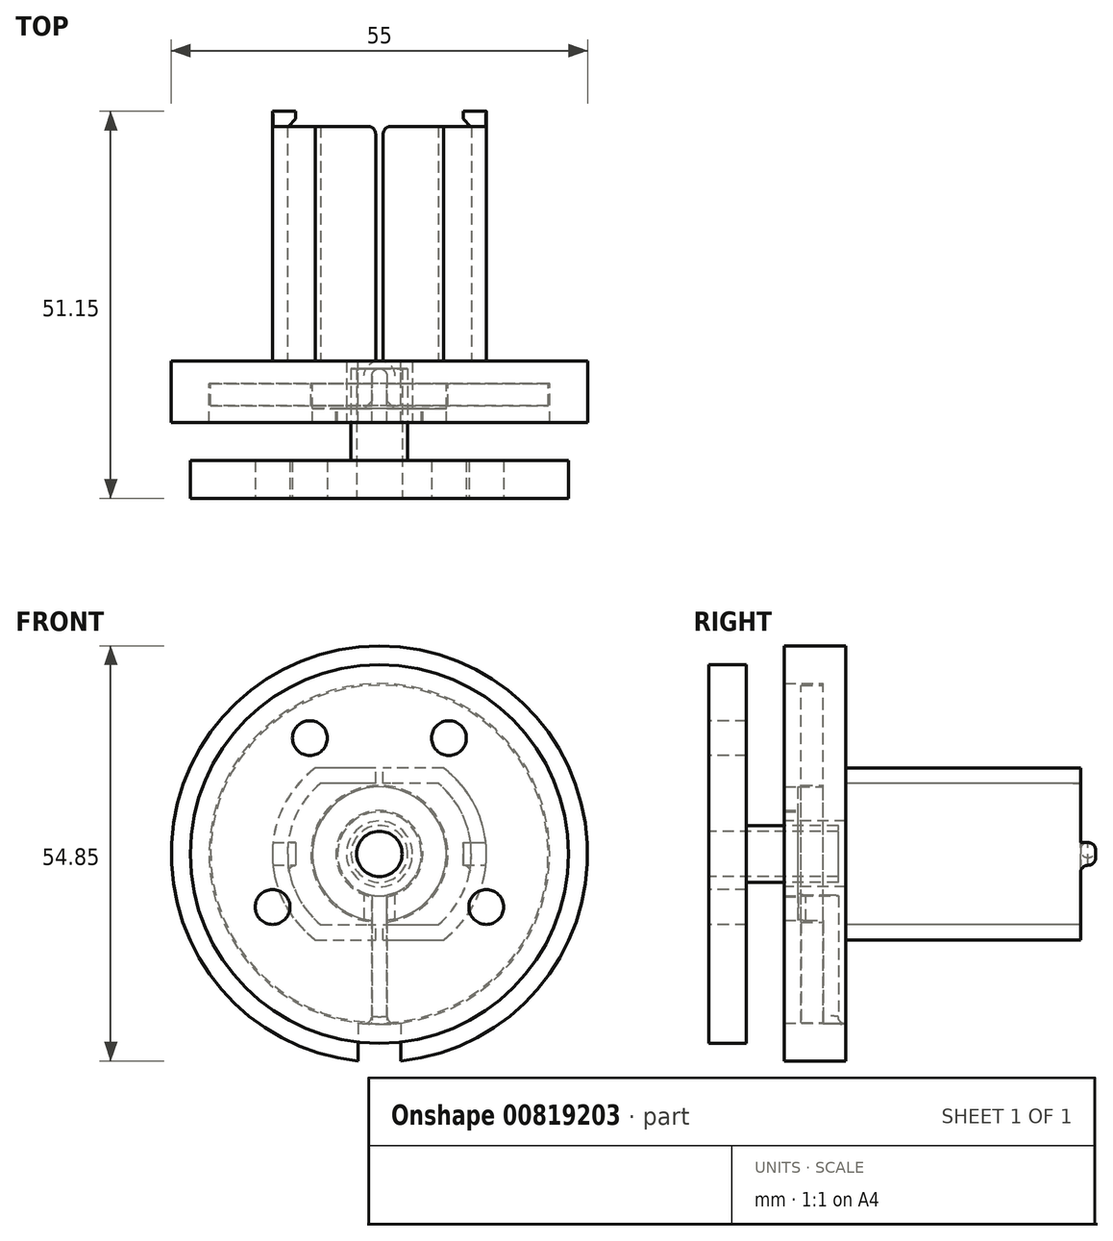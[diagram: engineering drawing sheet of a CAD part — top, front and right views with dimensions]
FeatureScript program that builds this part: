
annotation { "Feature Type Name" : "Feature", "Feature Type Description" : "" }
export const myFeature = defineFeature(function(context is Context, id is Id, definition is map)
    precondition{}
    {
        {
            var Q0;
            Q0=qCreatedBy(makeId("Front.planeOp"),FACE);
            var sketch = newSketch(context, id + "F0", { "sketchPlane" : qUnion([Q0])});
            skCircle(sketch, "E0", {"center": v(-32.51, 36.23) * mm, "radius": 22.3 * mm});
            skCircle(sketch, "E1", {"center": v(-32.51, 36.23) * mm, "radius": 9.05 * mm});
            skCircle(sketch, "E2", {"center": v(-32.51, 36.23) * mm, "radius": 27.5 * mm});
            skSolve(sketch);
        }
        {
            var Q0;
            Q0=makeQuery(id+"F0.imprint","IMPRINT",FACE,{"disambiguationData":[TD([[makeQuery(id+"F0.imprint","IMPRINT",EDGE,{"derivedFrom":sQuery(id+"F0.wireOp",EDGE,"E0")}),1.0]])]});
            extrude(context, id + "F1", {"entities" : qUnion([Q0]), "depth" : 2.9 * mm, "offsetDistance" : 25 * mm});
        }
        {
            var Q0;
            Q0=makeQuery(id+"F1.opExtrude","CAP_FACE",FACE,{"disambiguationData":[OSD([sQuery(id+"F0.wireOp",EDGE,"E0"),sQuery(id+"F0.wireOp",EDGE,"E1")])],"isStart":false});
            cPlane(context, id + "F2", {"entities" : qUnion([Q0]), "cplaneType" : CPlaneType.OFFSET, "offset" : .4 * mm, "width" : 150 * mm, "height" : 150 * mm});
        }
        {
            var Q0;
            Q0=qCreatedBy(id+"F2.planeOp",FACE);
            var sketch = newSketch(context, id + "F3", { "sketchPlane" : qUnion([Q0])});
            skCircle(sketch, "E3.0", {"center": v(-32.51, 36.23) * mm, "radius": 9.05 * mm});
            skCircle(sketch, "E4", {"center": v(-32.51, 36.23) * mm, "radius": 12.7 * mm});
            skCircle(sketch, "E5", {"center": v(-32.51, 36.23) * mm, "radius": 5.75 * mm});
            skSolve(sketch);
        }
        {
            var Q0;
            Q0=makeQuery(id+"F3.imprint","IMPRINT",FACE,{"disambiguationData":[TD([[makeQuery(id+"F3.imprint","IMPRINT",EDGE,{"derivedFrom":sQuery(id+"F3.wireOp",EDGE,"E3.0")}),1.0]])]});
            var Q1;
            Q1=makeQuery(id+"F3.imprint","IMPRINT",FACE,{"disambiguationData":[TD([[makeQuery(id+"F3.imprint","IMPRINT",EDGE,{"derivedFrom":sQuery(id+"F3.wireOp",EDGE,"E3.0")}),-1.0]])]});
            extrude(context, id + "F4", {"entities" : qUnion([Q0, Q1]), "depth" : 1.85 * mm, "offsetDistance" : 25 * mm});
        }
        {
            var Q0;
            Q0=makeQuery(id+"F0.imprint","IMPRINT",FACE,{"disambiguationData":[TD([[makeQuery(id+"F0.imprint","IMPRINT",EDGE,{"derivedFrom":sQuery(id+"F0.wireOp",EDGE,"E0")}),-1.0]])]});
            var Q1;
            Q1=makeQuery(id+"F0.imprint","IMPRINT",FACE,{"disambiguationData":[TD([[makeQuery(id+"F0.imprint","IMPRINT",EDGE,{"derivedFrom":sQuery(id+"F0.wireOp",EDGE,"E0")}),1.0]])]});
            var Q2;
            Q2=makeQuery(id+"F0.imprint","IMPRINT",FACE,{"disambiguationData":[TD([[makeQuery(id+"F0.imprint","IMPRINT",EDGE,{"derivedFrom":sQuery(id+"F0.wireOp",EDGE,"E1")}),1.0]])]});
            var Q3;
            Q3=makeQuery(id+"F4.opExtrude","CAP_FACE",FACE,{"disambiguationData":[OSD([sQuery(id+"F3.wireOp",EDGE,"E4"),sQuery(id+"F3.wireOp",EDGE,"E5")])],"isStart":false});
            extrude(context, id + "F5", {"entities" : qUnion([Q0, Q1, Q2]), "endBound" : BoundingType.UP_TO_SURFACE, "depth" : 25 * mm, "endBoundEntityFace" : qUnion([Q3]), "offsetDistance" : 25 * mm, "hasSecondDirection" : true, "secondDirectionOppositeDirection" : true, "secondDirectionDepth" : 3 * mm});
        }
        {
            var Q0;
            Q0=makeQuery(id+"F1.opExtrude","SWEPT_BODY",BODY,{"disambiguationData":[OSD([sQuery(id+"F0.wireOp",EDGE,"E0"),sQuery(id+"F0.wireOp",EDGE,"E1")])]});
            var Q1;
            Q1=makeQuery(id+"F4.opExtrude","SWEPT_BODY",BODY,{"disambiguationData":[OSD([sQuery(id+"F3.wireOp",EDGE,"E4"),sQuery(id+"F3.wireOp",EDGE,"E5")])]});
            var Q2;
            Q2=makeQuery(id+"F5.opExtrude","SWEPT_BODY",BODY,{"disambiguationData":[OSD([sQuery(id+"F0.wireOp",EDGE,"E2")])]});
            var Q3;
            Q3=makeQuery(id+"F4.opExtrude","SWEPT_FACE",FACE,{"disambiguationData":[OSD([sQuery(id+"F3.wireOp",EDGE,"E5")])]});
            var Q4;
            Q4=makeQuery(id+"F4.opExtrude","SWEPT_FACE",FACE,{"disambiguationData":[OSD([sQuery(id+"F3.wireOp",EDGE,"E4")])]});
            var Q5;
            Q5=makeQuery(id+"F1.opExtrude","SWEPT_FACE",FACE,{"disambiguationData":[OSD([sQuery(id+"F0.wireOp",EDGE,"E0")])]});
            var Q6;
            Q6=makeQuery(id+"F1.opExtrude","SWEPT_FACE",FACE,{"disambiguationData":[OSD([sQuery(id+"F0.wireOp",EDGE,"E1")])]});
            booleanBodies(context, id + "F6", {"operationType" : BooleanOperationType.SUBTRACTION, "tools" : qUnion([Q0, Q1]), "targets" : qUnion([Q2]), "offset" : true, "entitiesToOffset" : qUnion([Q3, Q4, Q5, Q6]), "offsetDistance" : .2 * mm, "keepTools" : true});
        }
        {
            var Q0;
            Q0=makeQuery(id+"F6.opBoolean","COPY",FACE,{"derivedFrom":makeQuery(id+"F1.opExtrude","CAP_FACE",FACE,{"disambiguationData":[OSD([sQuery(id+"F0.wireOp",EDGE,"E0"),sQuery(id+"F0.wireOp",EDGE,"E1")])],"isStart":false})});
            var Q1;
            Q1=makeQuery(id+"F6.tempBoolean.opBoolean","COPY",FACE,{"derivedFrom":makeQuery(id+"F6.offsetTempBody.opPattern","COPY",FACE,{"derivedFrom":makeQuery(id+"F1.opExtrude","CAP_FACE",FACE,{"disambiguationData":[OSD([sQuery(id+"F0.wireOp",EDGE,"E0"),sQuery(id+"F0.wireOp",EDGE,"E1")])],"isStart":false}),"instanceName":"1"})});
            extrude(context, id + "F7", {"entities" : qUnion([Q0, Q1]), "operationType" : NewBodyOperationType.REMOVE, "endBound" : BoundingType.THROUGH_ALL, "oppositeDirection" : true, "depth" : 25 * mm, "offsetDistance" : 25 * mm});
        }
        {
            var Q0;
            Q0=makeQuery(id+"F6.tempBoolean.opBoolean","SPLIT",FACE,{"disambiguationData":[TD([makeQuery(id+"F6.offsetTempBody.opPattern","COPY",FACE,{"derivedFrom":makeQuery(id+"F4.opExtrude","SWEPT_FACE",FACE,{"disambiguationData":[OSD([sQuery(id+"F3.wireOp",EDGE,"E5")])]}),"instanceName":"1"})])],"derivedFrom":makeQuery(id+"F5.opExtrude","CAP_FACE",FACE,{"disambiguationData":[OSD([sQuery(id+"F0.wireOp",EDGE,"E2")])],"isStart":false})});
            var sketch = newSketch(context, id + "F8", { "sketchPlane" : qUnion([Q0])});
            skCircle(sketch, "E6.0", {"center": v(-32.51, 36.23) * mm, "radius": 5.55 * mm});
            skCircle(sketch, "E7", {"center": v(-32.51, 36.23) * mm, "radius": 4.35 * mm});
            skPoint(sketch, "E8", {"position": v(-36.86, 36.23) * mm});
            skPoint(sketch, "E9", {"position": v(-38.06, 36.23) * mm});
            skSolve(sketch);
        }
        {
            var Q0;
            Q0=makeQuery(id+"F8.imprint","IMPRINT",FACE,{"disambiguationData":[TD([[makeQuery(id+"F8.imprint","IMPRINT",EDGE,{"derivedFrom":sQuery(id+"F8.wireOp",EDGE,"E7")}),1.0]])]});
            extrude(context, id + "F9", {"entities" : qUnion([Q0]), "operationType" : NewBodyOperationType.REMOVE, "endBound" : BoundingType.THROUGH_ALL, "oppositeDirection" : true, "depth" : 25 * mm, "offsetDistance" : 25 * mm});
        }
        {
            var Q0;
            Q0=makeQuery(id+"F6.tempBoolean.opBoolean","SPLIT",FACE,{"disambiguationData":[TD([makeQuery(id+"F6.offsetTempBody.opPattern","COPY",FACE,{"derivedFrom":makeQuery(id+"F4.opExtrude","SWEPT_FACE",FACE,{"disambiguationData":[OSD([sQuery(id+"F3.wireOp",EDGE,"E5")])]}),"instanceName":"1"})])],"derivedFrom":makeQuery(id+"F5.opExtrude","CAP_FACE",FACE,{"disambiguationData":[OSD([sQuery(id+"F0.wireOp",EDGE,"E2")])],"isStart":false})});
            var sketch = newSketch(context, id + "F10", { "sketchPlane" : qUnion([Q0])});
            skCircle(sketch, "E10.0", {"center": v(-32.51, 36.23) * mm, "radius": 4.35 * mm});
            skCircle(sketch, "E11", {"center": v(-32.51, 36.23) * mm, "radius": 3 * mm});
            skCircle(sketch, "E12", {"center": v(-32.51, 36.23) * mm, "radius": 3.75 * mm});
            skPoint(sketch, "E13", {"position": v(-35.51, 36.23) * mm});
            skPoint(sketch, "E14", {"position": v(-36.26, 36.23) * mm});
            skPoint(sketch, "E15", {"position": v(-36.86, 36.23) * mm});
            skSolve(sketch);
        }
        {
            var Q0;
            Q0=makeQuery(id+"F10.imprint","IMPRINT",FACE,{"disambiguationData":[TD([[makeQuery(id+"F10.imprint","IMPRINT",EDGE,{"derivedFrom":sQuery(id+"F10.wireOp",EDGE,"E11")}),-1.0]])]});
            var Q1;
            Q1=makeQuery(id+"F5.opExtrude","CAP_FACE",FACE,{"disambiguationData":[OSD([sQuery(id+"F0.wireOp",EDGE,"E2")])],"isStart":true});
            extrude(context, id + "F11", {"entities" : qUnion([Q0]), "endBound" : BoundingType.UP_TO_SURFACE, "oppositeDirection" : true, "depth" : 25 * mm, "endBoundEntityFace" : qUnion([Q1]), "hasOffset" : true, "offsetDistance" : 1 * mm, "hasSecondDirection" : true, "secondDirectionOppositeDirection" : false, "secondDirectionDepth" : 5 * mm});
        }
        {
            var Q0;
            Q0=makeQuery(id+"F11.opExtrude","CAP_FACE",FACE,{"disambiguationData":[OSD([sQuery(id+"F10.wireOp",EDGE,"E11"),sQuery(id+"F10.wireOp",EDGE,"E12")])],"isStart":true});
            var sketch = newSketch(context, id + "F12", { "sketchPlane" : qUnion([Q0])});
            skCircle(sketch, "E16.0", {"center": v(-32.51, 36.23) * mm, "radius": 3 * mm});
            skCircle(sketch, "E17", {"center": v(-32.51, 36.23) * mm, "radius": 25 * mm});
            skSolve(sketch);
        }
        {
            var Q0;
            Q0=makeQuery(id+"F12.imprint","IMPRINT",FACE,{"disambiguationData":[TD([[makeQuery(id+"F12.imprint","IMPRINT",EDGE,{"derivedFrom":sQuery(id+"F12.wireOp",EDGE,"E17")}),1.0]])]});
            var Q1;
            Q1=makeQuery(id+"F12.imprint","IMPRINT",FACE,{"disambiguationData":[TD([[makeQuery(id+"F12.imprint","IMPRINT",EDGE,{"derivedFrom":sQuery(id+"F12.wireOp",EDGE,"E16.0")}),-1.0]])]});
            extrude(context, id + "F13", {"entities" : qUnion([Q0, Q1]), "operationType" : NewBodyOperationType.ADD, "depth" : 5 * mm, "offsetDistance" : 25 * mm});
        }
        {
            var Q0;
            Q0=makeQuery(id+"F13.opExtrude","CAP_FACE",FACE,{"disambiguationData":[OSD([sQuery(id+"F12.wireOp",EDGE,"E16.0"),sQuery(id+"F12.wireOp",EDGE,"E17")])],"isStart":false});
            var sketch = newSketch(context, id + "F14", { "sketchPlane" : qUnion([Q0])});
            skCircle(sketch, "E18", {"center": v(-41.7, 51.54) * mm, "radius": 2.3 * mm});
            skCircle(sketch, "E19", {"center": v(-23.32, 51.54) * mm, "radius": 2.3 * mm});
            skCircle(sketch, "E20", {"center": v(-46.63, 29.22) * mm, "radius": 2.3 * mm});
            skCircle(sketch, "E21", {"center": v(-18.4, 29.22) * mm, "radius": 2.3 * mm});
            skLineSegment(sketch, "E22", {"start": v(-46.63, 29.22) * mm, "end": v(-18.4, 29.22) * mm, "construction": true});
            skLineSegment(sketch, "E23", {"start": v(-41.7, 51.54) * mm, "end": v(-23.32, 51.54) * mm, "construction": true});
            skPoint(sketch, "E24", {"position": v(-32.51, 51.54) * mm});
            skPoint(sketch, "E25", {"position": v(-32.51, 29.22) * mm});
            skCircle(sketch, "E26.0", {"center": v(-32.51, 36.23) * mm, "radius": 3 * mm});
            skSolve(sketch);
        }
        {
            var Q0;
            Q0=makeQuery(id+"F14.imprint","IMPRINT",FACE,{"disambiguationData":[TD([[makeQuery(id+"F14.imprint","IMPRINT",EDGE,{"derivedFrom":sQuery(id+"F14.wireOp",EDGE,"E20")}),1.0]])]});
            var Q1;
            Q1=makeQuery(id+"F14.imprint","IMPRINT",FACE,{"disambiguationData":[TD([[makeQuery(id+"F14.imprint","IMPRINT",EDGE,{"derivedFrom":sQuery(id+"F14.wireOp",EDGE,"E18")}),1.0]])]});
            var Q2;
            Q2=makeQuery(id+"F14.imprint","IMPRINT",FACE,{"disambiguationData":[TD([[makeQuery(id+"F14.imprint","IMPRINT",EDGE,{"derivedFrom":sQuery(id+"F14.wireOp",EDGE,"E19")}),1.0]])]});
            var Q3;
            Q3=makeQuery(id+"F14.imprint","IMPRINT",FACE,{"disambiguationData":[TD([[makeQuery(id+"F14.imprint","IMPRINT",EDGE,{"derivedFrom":sQuery(id+"F14.wireOp",EDGE,"E21")}),1.0]])]});
            extrude(context, id + "F15", {"entities" : qUnion([Q0, Q1, Q2, Q3]), "operationType" : NewBodyOperationType.REMOVE, "endBound" : BoundingType.UP_TO_NEXT, "oppositeDirection" : true, "depth" : 25 * mm, "offsetDistance" : 25 * mm});
        }
        {
            var Q0;
            Q0=qCreatedBy(makeId("Top.planeOp"),FACE);
            var sketch = newSketch(context, id + "F16", { "sketchPlane" : qUnion([Q0])});
            skLineSegment(sketch, "E27.bottom", {"start": v(-35.34, -7.22) * mm, "end": v(-29.7, -7.22) * mm});
            skLineSegment(sketch, "E27.top", {"start": v(-35.34, 5.14) * mm, "end": v(-29.7, 5.14) * mm});
            skLineSegment(sketch, "E27.left", {"start": v(-35.34, -7.22) * mm, "end": v(-35.34, 5.14) * mm});
            skLineSegment(sketch, "E27.right", {"start": v(-29.7, -7.22) * mm, "end": v(-29.7, 5.14) * mm});
            skLineSegment(sketch, "E28.0", {"start": v(-5.01, -5.15) * mm, "end": v(-60.01, -5.15) * mm});
            skPoint(sketch, "E29", {"position": v(-32.51, -5.15) * mm});
            skPoint(sketch, "E30", {"position": v(-32.51, -7.22) * mm});
            skSolve(sketch);
        }
        {
            var Q0;
            {var subQ0=sQuery(id+"F16.wireOp",EDGE,"E27.top");Q0=makeQuery(id+"F16.imprint","IMPRINT",FACE,{"disambiguationData":[TD([[makeQuery(id+"F16.imprint","IMPRINT",EDGE,{"derivedFrom":subQ0}),-1.0]])]});}
            var Q1;
            {var subQ0=sQuery(id+"F0.wireOp",EDGE,"E0");Q1=makeQuery(id+"F7.boolean.opBoolean","MERGE",FACE,{"derivedFrom":[makeQuery(id+"F6.tempBoolean.opBoolean","COPY",FACE,{"derivedFrom":makeQuery(id+"F6.offsetTempBody.opPattern","COPY",FACE,{"derivedFrom":makeQuery(id+"F1.opExtrude","SWEPT_FACE",FACE,{"disambiguationData":[OSD([subQ0])]}),"instanceName":"1"})}),makeQuery(id+"F7.opExtrude","SWEPT_FACE",FACE,{"disambiguationData":[OSD([subQ0])]})]});}
            extrude(context, id + "F17", {"entities" : qUnion([Q0]), "operationType" : NewBodyOperationType.REMOVE, "endBound" : BoundingType.UP_TO_SURFACE, "depth" : 20 * mm, "endBoundEntityFace" : qUnion([Q1]), "offsetDistance" : 25 * mm});
        }
        {
            var Q0;
            Q0=makeQuery(id+"F5.opExtrude","CAP_FACE",FACE,{"disambiguationData":[OSD([sQuery(id+"F0.wireOp",EDGE,"E2")])],"isStart":true});
            var sketch = newSketch(context, id + "F18", { "sketchPlane" : qUnion([Q0])});
            skArc(sketch, "E31", {"start": v(40.27, 26.88) * mm, "mid": v(44.66, 36.23) * mm, "end": v(40.27, 45.58) * mm});
            skLineSegment(sketch, "E32", {"start": v(40.27, 26.88) * mm, "end": v(24.75, 26.88) * mm});
            skLineSegment(sketch, "E33", {"start": v(24.75, 45.58) * mm, "end": v(40.27, 45.58) * mm});
            skArc(sketch, "E34.trimOffspring", {"start": v(24.75, 45.58) * mm, "mid": v(20.36, 36.23) * mm, "end": v(24.75, 26.88) * mm});
            skLineSegment(sketch, "E35.0", {"start": v(40.96, 24.88) * mm, "end": v(24.06, 24.88) * mm});
            skArc(sketch, "E35.1", {"start": v(40.96, 24.88) * mm, "mid": v(46.66, 36.23) * mm, "end": v(40.96, 47.58) * mm});
            skLineSegment(sketch, "E35.2", {"start": v(24.06, 47.58) * mm, "end": v(40.96, 47.58) * mm});
            skArc(sketch, "E35.3", {"start": v(24.06, 47.58) * mm, "mid": v(18.36, 36.23) * mm, "end": v(24.06, 24.88) * mm});
            skLineSegment(sketch, "E36", {"start": v(32.51, 24.88) * mm, "end": v(32.51, 47.58) * mm, "construction": true});
            skArc(sketch, "E37.0.startCap", {"start": v(33.01, 24.88) * mm, "mid": v(32.51, 24.38) * mm, "end": v(32.01, 24.88) * mm, "construction": true});
            skArc(sketch, "E37.0.endCap", {"start": v(32.01, 47.58) * mm, "mid": v(32.51, 48.08) * mm, "end": v(33.01, 47.58) * mm, "construction": true});
            skLineSegment(sketch, "E37.0.left", {"start": v(32.01, 24.88) * mm, "end": v(32.01, 47.58) * mm});
            skLineSegment(sketch, "E37.0.right", {"start": v(33.01, 24.88) * mm, "end": v(33.01, 47.58) * mm});
            skSolve(sketch);
        }
        {
            var Q0;
            Q0=makeQuery(id+"F18.imprint","IMPRINT",FACE,{"disambiguationData":[TD([[makeQuery(id+"F18.imprint","IMPRINT",EDGE,{"derivedFrom":sQuery(id+"F18.wireOp",EDGE,"E31")}),-1.0]])]});
            var Q1;
            {var subQ4=sQuery(id+"F18.wireOp",EDGE,"E34.trimOffspring");Q1=makeQuery(id+"F18.imprint","IMPRINT",FACE,{"disambiguationData":[TD([[makeQuery(id+"F18.imprint","IMPRINT",EDGE,{"derivedFrom":subQ4}),-1.0]])]});}
            extrude(context, id + "F19", {"entities" : qUnion([Q0, Q1]), "operationType" : NewBodyOperationType.ADD, "depth" : 31 * mm, "offsetDistance" : 25 * mm});
        }
        {
            var Q0;
            Q0=makeQuery(id+"F19.opExtrude","CAP_FACE",FACE,{"disambiguationData":[OSD([sQuery(id+"F18.wireOp",EDGE,"E31"),sQuery(id+"F18.wireOp",EDGE,"E32"),sQuery(id+"F18.wireOp",EDGE,"E33"),sQuery(id+"F18.wireOp",EDGE,"E35.0"),sQuery(id+"F18.wireOp",EDGE,"E35.1"),sQuery(id+"F18.wireOp",EDGE,"E35.2"),sQuery(id+"F18.wireOp",EDGE,"E37.0.right")])],"isStart":false});
            var sketch = newSketch(context, id + "F20", { "sketchPlane" : qUnion([Q0])});
            skArc(sketch, "E38.0", {"start": v(24.06, 47.58) * mm, "mid": v(18.36, 36.23) * mm, "end": v(24.06, 24.88) * mm});
            skArc(sketch, "E38.1", {"start": v(40.96, 24.88) * mm, "mid": v(46.66, 36.23) * mm, "end": v(40.96, 47.58) * mm});
            skLineSegment(sketch, "E39", {"start": v(46.66, 36.23) * mm, "end": v(43.57, 36.23) * mm, "construction": true});
            skArc(sketch, "E40.0.startCap", {"start": v(46.66, 37.73) * mm, "mid": v(48.16, 36.23) * mm, "end": v(46.66, 34.73) * mm, "construction": true});
            skArc(sketch, "E40.0.endCap", {"start": v(18.36, 34.73) * mm, "mid": v(16.86, 36.23) * mm, "end": v(18.36, 37.73) * mm, "construction": true});
            skLineSegment(sketch, "E40.0.left", {"start": v(46.66, 34.73) * mm, "end": v(43.57, 34.73) * mm});
            skLineSegment(sketch, "E40.0.right", {"start": v(46.66, 37.73) * mm, "end": v(43.57, 37.73) * mm});
            skLineSegment(sketch, "E41.left", {"start": v(43.57, 37.73) * mm, "end": v(43.57, 34.73) * mm});
            skLineSegment(sketch, "E41.right", {"start": v(21.46, 37.73) * mm, "end": v(21.46, 34.73) * mm});
            skLineSegment(sketch, "E42.trimOffspring", {"start": v(21.46, 34.73) * mm, "end": v(18.36, 34.73) * mm});
            skLineSegment(sketch, "E43.trimOffspring", {"start": v(21.46, 37.73) * mm, "end": v(18.36, 37.73) * mm});
            skLineSegment(sketch, "E44.trimOffspring", {"start": v(21.46, 36.23) * mm, "end": v(18.36, 36.23) * mm, "construction": true});
            skPoint(sketch, "E45", {"position": v(44.57, 34.73) * mm});
            skSolve(sketch);
        }
        {
            var Q0;
            {var subQ0=sQuery(id+"F20.wireOp",EDGE,"E41.left");Q0=makeQuery(id+"F20.imprint","IMPRINT",FACE,{"disambiguationData":[TD([[makeQuery(id+"F20.imprint","IMPRINT",EDGE,{"derivedFrom":subQ0}),1.0]])]});}
            var Q1;
            {var subQ0=sQuery(id+"F20.wireOp",EDGE,"E40.0.left");var subQ1=sQuery(id+"F20.wireOp",EDGE,"E38.1");var subQ2=makeQuery(id+"F20.imprint","INTERSECT",VERTEX,{"derivedFrom":[subQ1,subQ0]});Q1=makeQuery(id+"F20.imprint","IMPRINT",FACE,{"disambiguationData":[TD([[makeQuery(id+"F20.imprint","IMPRINT",EDGE,{"disambiguationData":[TD([[subQ2,-1.0]])],"derivedFrom":subQ1}),1.0]])]});}
            var Q2;
            {var subQ5=sQuery(id+"F20.wireOp",EDGE,"E41.right");Q2=makeQuery(id+"F20.imprint","IMPRINT",FACE,{"disambiguationData":[TD([[makeQuery(id+"F20.imprint","IMPRINT",EDGE,{"derivedFrom":subQ5}),-1.0]])]});}
            extrude(context, id + "F21", {"entities" : qUnion([Q0, Q1, Q2]), "operationType" : NewBodyOperationType.ADD, "depth" : 2 * mm, "offsetDistance" : 25 * mm});
        }
        {
            var Q0;
            Q0=makeQuery(id+"F21.opExtrude","CAP_EDGE",EDGE,{"disambiguationData":[OSD([sQuery(id+"F20.wireOp",EDGE,"E41.left")])],"isStart":true});
            var Q1;
            Q1=makeQuery(id+"F21.opExtrude","CAP_EDGE",EDGE,{"disambiguationData":[OSD([sQuery(id+"F20.wireOp",EDGE,"E41.right")])],"isStart":true});
            chamfer(context, id + "F22", {"entities" : qUnion([Q0, Q1]), "width" : 1 * mm, "tangentPropagation" : true});
        }
        {
            var Q0;
            {var subQ0=sQuery(id+"F20.wireOp",EDGE,"E40.0.right");Q0=makeQuery(id+"F21.boolean.opBoolean","SPLIT",EDGE,{"disambiguationData":[topologyDisambiguationEdgeConnected([makeQuery(id+"F19.opExtrude","CAP_FACE",FACE,{"disambiguationData":[OSD([sQuery(id+"F18.wireOp",EDGE,"E31"),sQuery(id+"F18.wireOp",EDGE,"E32"),sQuery(id+"F18.wireOp",EDGE,"E33"),sQuery(id+"F18.wireOp",EDGE,"E35.0"),sQuery(id+"F18.wireOp",EDGE,"E35.1"),sQuery(id+"F18.wireOp",EDGE,"E35.2"),sQuery(id+"F18.wireOp",EDGE,"E37.0.right")])],"isStart":false})])],"derivedFrom":makeQuery(id+"F21.opExtrude","CAP_EDGE",EDGE,{"disambiguationData":[OSD([subQ0])],"isStart":true})});}
            var Q1;
            {var subQ0=sQuery(id+"F20.wireOp",EDGE,"E43.trimOffspring");Q1=makeQuery(id+"F21.boolean.opBoolean","SPLIT",EDGE,{"disambiguationData":[topologyDisambiguationEdgeConnected([makeQuery(id+"F19.opExtrude","CAP_FACE",FACE,{"disambiguationData":[OSD([sQuery(id+"F18.wireOp",EDGE,"E32"),sQuery(id+"F18.wireOp",EDGE,"E33"),sQuery(id+"F18.wireOp",EDGE,"E34.trimOffspring"),sQuery(id+"F18.wireOp",EDGE,"E35.0"),sQuery(id+"F18.wireOp",EDGE,"E35.2"),sQuery(id+"F18.wireOp",EDGE,"E35.3"),sQuery(id+"F18.wireOp",EDGE,"E37.0.left")])],"isStart":false})])],"derivedFrom":makeQuery(id+"F21.opExtrude","CAP_EDGE",EDGE,{"disambiguationData":[OSD([subQ0])],"isStart":true})});}
            var Q2;
            {var subQ0=sQuery(id+"F20.wireOp",EDGE,"E42.trimOffspring");Q2=makeQuery(id+"F21.boolean.opBoolean","SPLIT",EDGE,{"disambiguationData":[topologyDisambiguationEdgeConnected([makeQuery(id+"F19.opExtrude","CAP_FACE",FACE,{"disambiguationData":[OSD([sQuery(id+"F18.wireOp",EDGE,"E32"),sQuery(id+"F18.wireOp",EDGE,"E33"),sQuery(id+"F18.wireOp",EDGE,"E34.trimOffspring"),sQuery(id+"F18.wireOp",EDGE,"E35.0"),sQuery(id+"F18.wireOp",EDGE,"E35.2"),sQuery(id+"F18.wireOp",EDGE,"E35.3"),sQuery(id+"F18.wireOp",EDGE,"E37.0.left")])],"isStart":false})])],"derivedFrom":makeQuery(id+"F21.opExtrude","CAP_EDGE",EDGE,{"disambiguationData":[OSD([subQ0])],"isStart":true})});}
            var Q3;
            {var subQ0=sQuery(id+"F20.wireOp",EDGE,"E40.0.left");Q3=makeQuery(id+"F21.boolean.opBoolean","SPLIT",EDGE,{"disambiguationData":[topologyDisambiguationEdgeConnected([makeQuery(id+"F19.opExtrude","CAP_FACE",FACE,{"disambiguationData":[OSD([sQuery(id+"F18.wireOp",EDGE,"E31"),sQuery(id+"F18.wireOp",EDGE,"E32"),sQuery(id+"F18.wireOp",EDGE,"E33"),sQuery(id+"F18.wireOp",EDGE,"E35.0"),sQuery(id+"F18.wireOp",EDGE,"E35.1"),sQuery(id+"F18.wireOp",EDGE,"E35.2"),sQuery(id+"F18.wireOp",EDGE,"E37.0.right")])],"isStart":false})])],"derivedFrom":makeQuery(id+"F21.opExtrude","CAP_EDGE",EDGE,{"disambiguationData":[OSD([subQ0])],"isStart":true})});}
            var Q4;
            Q4=makeQuery(id+"F21.opExtrude","CAP_EDGE",EDGE,{"disambiguationData":[OSD([sQuery(id+"F20.wireOp",EDGE,"E40.0.left")])],"isStart":false});
            var Q5;
            Q5=makeQuery(id+"F21.opExtrude","CAP_EDGE",EDGE,{"disambiguationData":[OSD([sQuery(id+"F20.wireOp",EDGE,"E40.0.right")])],"isStart":false});
            var Q6;
            Q6=makeQuery(id+"F21.opExtrude","CAP_EDGE",EDGE,{"disambiguationData":[OSD([sQuery(id+"F20.wireOp",EDGE,"E42.trimOffspring")])],"isStart":false});
            var Q7;
            Q7=makeQuery(id+"F21.opExtrude","CAP_EDGE",EDGE,{"disambiguationData":[OSD([sQuery(id+"F20.wireOp",EDGE,"E43.trimOffspring")])],"isStart":false});
            var Q8;
            {var subQ0=sQuery(id+"F18.wireOp",EDGE,"E37.0.right");Q8=makeQuery(id+"F19.opExtrude","CAP_EDGE",EDGE,{"disambiguationData":[OSD([subQ0]),TDD([makeQuery(id+"F18.imprint","IMPRINT",EDGE,{"disambiguationData":[TD([[makeQuery(id+"F18.imprint","INTERSECT",VERTEX,{"derivedFrom":[sQuery(id+"F18.wireOp",EDGE,"E35.0"),subQ0]}),-1.0]])],"derivedFrom":subQ0})])],"isStart":false});}
            var Q9;
            {var subQ0=sQuery(id+"F18.wireOp",EDGE,"E37.0.left");Q9=makeQuery(id+"F19.opExtrude","CAP_EDGE",EDGE,{"disambiguationData":[OSD([subQ0]),TDD([makeQuery(id+"F18.imprint","IMPRINT",EDGE,{"disambiguationData":[TD([[makeQuery(id+"F18.imprint","INTERSECT",VERTEX,{"derivedFrom":[sQuery(id+"F18.wireOp",EDGE,"E35.0"),subQ0]}),-1.0]])],"derivedFrom":subQ0})])],"isStart":false});}
            var Q10;
            {var subQ0=sQuery(id+"F18.wireOp",EDGE,"E37.0.left");Q10=makeQuery(id+"F19.opExtrude","CAP_EDGE",EDGE,{"disambiguationData":[OSD([subQ0]),TDD([makeQuery(id+"F18.imprint","IMPRINT",EDGE,{"disambiguationData":[TD([[makeQuery(id+"F18.imprint","INTERSECT",VERTEX,{"derivedFrom":[sQuery(id+"F18.wireOp",EDGE,"E35.2"),subQ0]}),1.0]])],"derivedFrom":subQ0})])],"isStart":false});}
            var Q11;
            {var subQ0=sQuery(id+"F18.wireOp",EDGE,"E37.0.right");Q11=makeQuery(id+"F19.opExtrude","CAP_EDGE",EDGE,{"disambiguationData":[OSD([subQ0]),TDD([makeQuery(id+"F18.imprint","IMPRINT",EDGE,{"disambiguationData":[TD([[makeQuery(id+"F18.imprint","INTERSECT",VERTEX,{"derivedFrom":[sQuery(id+"F18.wireOp",EDGE,"E35.2"),subQ0]}),1.0]])],"derivedFrom":subQ0})])],"isStart":false});}
            fillet(context, id + "F23", {"entities" : qUnion([Q0, Q1, Q2, Q3, Q4, Q5, Q6, Q7, Q8, Q9, Q10, Q11]), "radius" : 1 * mm, "tangentPropagation" : true, "allowEdgeOverflow" : false});
        }
        {
            var Q0;
            Q0=makeQuery(id+"F6.tempBoolean.opBoolean","SPLIT",FACE,{"disambiguationData":[TD([makeQuery(id+"F6.offsetTempBody.opPattern","COPY",FACE,{"derivedFrom":makeQuery(id+"F4.opExtrude","SWEPT_FACE",FACE,{"disambiguationData":[OSD([sQuery(id+"F3.wireOp",EDGE,"E5")])]}),"instanceName":"1"})])],"derivedFrom":makeQuery(id+"F5.opExtrude","CAP_FACE",FACE,{"disambiguationData":[OSD([sQuery(id+"F0.wireOp",EDGE,"E2")])],"isStart":false})});
            var sketch = newSketch(context, id + "F24", { "sketchPlane" : qUnion([Q0])});
            skPoint(sketch, "E46", {"position": v(-32.51, 30.77) * mm});
            skCircle(sketch, "E47.0", {"center": v(-32.51, 36.23) * mm, "radius": 8.85 * mm});
            skPoint(sketch, "E48", {"position": v(-32.51, 27.38) * mm});
            skArc(sketch, "E49.0", {"start": v(-35.34, 13.9) * mm, "mid": v(-32.51, 13.72) * mm, "end": v(-29.7, 13.9) * mm});
            skPoint(sketch, "E50", {"position": v(-32.51, 13.72) * mm});
            skLineSegment(sketch, "E51", {"start": v(-32.51, 30.77) * mm, "end": v(-32.51, 13.72) * mm, "construction": true});
            skArc(sketch, "E52.0.startCap", {"start": v(-33.51, 30.77) * mm, "mid": v(-32.51, 31.77) * mm, "end": v(-31.51, 30.77) * mm, "construction": true});
            skArc(sketch, "E52.0.endCap", {"start": v(-31.51, 13.72) * mm, "mid": v(-32.51, 12.72) * mm, "end": v(-33.51, 13.72) * mm, "construction": true});
            skLineSegment(sketch, "E52.0.left", {"start": v(-31.51, 30.77) * mm, "end": v(-31.51, 13.72) * mm});
            skLineSegment(sketch, "E52.0.right", {"start": v(-33.51, 30.77) * mm, "end": v(-33.51, 13.72) * mm});
            skCircle(sketch, "E53.0", {"center": v(-32.51, 36.23) * mm, "radius": 5.55 * mm});
            skSolve(sketch);
        }
        {
            var Q0;
            {var subQ0=sQuery(id+"F24.wireOp",EDGE,"E52.0.startCap");Q0=makeQuery(id+"F24.imprint","IMPRINT",FACE,{"disambiguationData":[TD([[makeQuery(id+"F24.imprint","IMPRINT",EDGE,{"derivedFrom":subQ0}),-1.0]])]});}
            var Q1;
            {var subQ0=sQuery(id+"F24.wireOp",EDGE,"E52.0.left");var subQ1=makeQuery(id+"F9.boolean.opBoolean","COPY",EDGE,{"derivedFrom":makeQuery(id+"F9.opExtrude","CAP_EDGE",EDGE,{"disambiguationData":[OSD([sQuery(id+"F8.wireOp",EDGE,"E7")])],"isStart":true})});var subQ2=makeQuery(id+"F24.imprint","INTERSECT",VERTEX,{"derivedFrom":[subQ1,subQ0]});Q1=makeQuery(id+"F24.imprint","IMPRINT",FACE,{"disambiguationData":[TD([[makeQuery(id+"F24.imprint","IMPRINT",EDGE,{"disambiguationData":[TD([[subQ2,-1.0]])],"derivedFrom":subQ0}),-1.0]])]});}
            var Q2;
            {var subQ0=sQuery(id+"F24.wireOp",EDGE,"E52.0.left");var subQ1=sQuery(id+"F24.wireOp",EDGE,"E47.0");var subQ2=makeQuery(id+"F24.imprint","INTERSECT",VERTEX,{"derivedFrom":[subQ1,subQ0]});Q2=makeQuery(id+"F24.imprint","IMPRINT",FACE,{"disambiguationData":[TD([[makeQuery(id+"F24.imprint","IMPRINT",EDGE,{"disambiguationData":[TD([[subQ2,1.0]])],"derivedFrom":subQ1}),1.0]])]});}
            var Q3;
            {var subQ0=sQuery(id+"F24.wireOp",EDGE,"E52.0.left");var subQ1=sQuery(id+"F24.wireOp",EDGE,"E47.0");var subQ2=makeQuery(id+"F24.imprint","INTERSECT",VERTEX,{"derivedFrom":[subQ1,subQ0]});Q3=makeQuery(id+"F24.imprint","IMPRINT",FACE,{"disambiguationData":[TD([[makeQuery(id+"F24.imprint","IMPRINT",EDGE,{"disambiguationData":[TD([[subQ2,1.0]])],"derivedFrom":subQ1}),-1.0]])]});}
            var Q4;
            Q4=makeQuery(id+"F6.tempBoolean.opBoolean","COPY",FACE,{"derivedFrom":makeQuery(id+"F6.offsetTempBody.opPattern","COPY",FACE,{"derivedFrom":makeQuery(id+"F1.opExtrude","CAP_FACE",FACE,{"disambiguationData":[OSD([sQuery(id+"F0.wireOp",EDGE,"E0"),sQuery(id+"F0.wireOp",EDGE,"E1")])],"isStart":true}),"instanceName":"1"})});
            extrude(context, id + "F25", {"entities" : qUnion([Q0, Q1, Q2, Q3]), "operationType" : NewBodyOperationType.REMOVE, "endBound" : BoundingType.UP_TO_SURFACE, "oppositeDirection" : true, "depth" : 25 * mm, "endBoundEntityFace" : qUnion([Q4]), "hasOffset" : true, "offsetDistance" : 2 * mm, "offsetOppositeDirection" : true});
        }
        {
            var Q0;
            Q0=makeQuery(id+"F25.boolean.opBoolean","COPY",EDGE,{"derivedFrom":makeQuery(id+"F25.opExtrude","CAP_EDGE",EDGE,{"disambiguationData":[OSD([sQuery(id+"F24.wireOp",EDGE,"E52.0.left")])],"isStart":false})});
            var Q1;
            Q1=makeQuery(id+"F25.boolean.opBoolean","COPY",EDGE,{"derivedFrom":makeQuery(id+"F25.opExtrude","CAP_EDGE",EDGE,{"disambiguationData":[OSD([sQuery(id+"F24.wireOp",EDGE,"E52.0.right")])],"isStart":false})});
            fillet(context, id + "F26", {"entities" : qUnion([Q0, Q1]), "radius" : 1 * mm, "tangentPropagation" : true, "allowEdgeOverflow" : false});
        }
        {
            var Q0;
            Q0=makeQuery(id+"F25.boolean.opBoolean","INTERSECT",EDGE,{"derivedFrom":[makeQuery(id+"F6.tempBoolean.opBoolean","COPY",FACE,{"derivedFrom":makeQuery(id+"F6.offsetTempBody.opPattern","COPY",FACE,{"derivedFrom":makeQuery(id+"F4.opExtrude","CAP_FACE",FACE,{"disambiguationData":[OSD([sQuery(id+"F3.wireOp",EDGE,"E4"),sQuery(id+"F3.wireOp",EDGE,"E5")])],"isStart":true}),"instanceName":"1"})}),makeQuery(id+"F25.opExtrude","SWEPT_FACE",FACE,{"disambiguationData":[OSD([sQuery(id+"F24.wireOp",EDGE,"E52.0.left")])]})]});
            var Q1;
            Q1=makeQuery(id+"F25.boolean.opBoolean","INTERSECT",EDGE,{"derivedFrom":[makeQuery(id+"F6.tempBoolean.opBoolean","COPY",FACE,{"derivedFrom":makeQuery(id+"F6.offsetTempBody.opPattern","COPY",FACE,{"derivedFrom":makeQuery(id+"F4.opExtrude","CAP_FACE",FACE,{"disambiguationData":[OSD([sQuery(id+"F3.wireOp",EDGE,"E4"),sQuery(id+"F3.wireOp",EDGE,"E5")])],"isStart":true}),"instanceName":"1"})}),makeQuery(id+"F25.opExtrude","SWEPT_FACE",FACE,{"disambiguationData":[OSD([sQuery(id+"F24.wireOp",EDGE,"E52.0.right")])]})]});
            chamfer(context, id + "F27", {"entities" : qUnion([Q0, Q1]), "width" : 1 * mm, "tangentPropagation" : true});
        }
        {
            var Q0;
            Q0=makeQuery(id+"F25.boolean.opBoolean","COPY",EDGE,{"derivedFrom":makeQuery(id+"F25.opExtrude","SWEPT_EDGE",EDGE,{"disambiguationData":[OSD([sQuery(id+"F24.wireOp",EDGE,"E49.0"),sQuery(id+"F24.wireOp",EDGE,"E52.0.left")])]})});
            var Q1;
            Q1=makeQuery(id+"F26.opFillet","BLEND_EDGE",EDGE,{"blendedFrom":[makeQuery(id+"F25.boolean.opBoolean","COPY",EDGE,{"derivedFrom":makeQuery(id+"F25.opExtrude","CAP_EDGE",EDGE,{"disambiguationData":[OSD([sQuery(id+"F24.wireOp",EDGE,"E52.0.left")])],"isStart":false})}),makeQuery(id+"F17.boolean.opBoolean","COPY",FACE,{"derivedFrom":makeQuery(id+"F17.opExtrude","CAP_FACE",FACE,{"disambiguationData":[OSD([sQuery(id+"F16.wireOp",EDGE,"E27.top"),sQuery(id+"F16.wireOp",EDGE,"E27.left"),sQuery(id+"F16.wireOp",EDGE,"E27.right"),sQuery(id+"F16.wireOp",EDGE,"E28.0")])],"isStart":false})})],"blendedInto":[makeQuery(id+"F17.boolean.opBoolean","COPY",FACE,{"derivedFrom":makeQuery(id+"F17.opExtrude","CAP_FACE",FACE,{"disambiguationData":[OSD([sQuery(id+"F16.wireOp",EDGE,"E27.top"),sQuery(id+"F16.wireOp",EDGE,"E27.left"),sQuery(id+"F16.wireOp",EDGE,"E27.right"),sQuery(id+"F16.wireOp",EDGE,"E28.0")])],"isStart":false})})]});
            var Q2;
            Q2=makeQuery(id+"F26.opFillet","BLEND_EDGE",EDGE,{"blendedFrom":[makeQuery(id+"F25.boolean.opBoolean","COPY",EDGE,{"derivedFrom":makeQuery(id+"F25.opExtrude","CAP_EDGE",EDGE,{"disambiguationData":[OSD([sQuery(id+"F24.wireOp",EDGE,"E52.0.right")])],"isStart":false})}),makeQuery(id+"F17.boolean.opBoolean","COPY",FACE,{"derivedFrom":makeQuery(id+"F17.opExtrude","CAP_FACE",FACE,{"disambiguationData":[OSD([sQuery(id+"F16.wireOp",EDGE,"E27.top"),sQuery(id+"F16.wireOp",EDGE,"E27.left"),sQuery(id+"F16.wireOp",EDGE,"E27.right"),sQuery(id+"F16.wireOp",EDGE,"E28.0")])],"isStart":false})})],"blendedInto":[makeQuery(id+"F17.boolean.opBoolean","COPY",FACE,{"derivedFrom":makeQuery(id+"F17.opExtrude","CAP_FACE",FACE,{"disambiguationData":[OSD([sQuery(id+"F16.wireOp",EDGE,"E27.top"),sQuery(id+"F16.wireOp",EDGE,"E27.left"),sQuery(id+"F16.wireOp",EDGE,"E27.right"),sQuery(id+"F16.wireOp",EDGE,"E28.0")])],"isStart":false})})]});
            var Q3;
            Q3=makeQuery(id+"F25.boolean.opBoolean","COPY",EDGE,{"derivedFrom":makeQuery(id+"F25.opExtrude","SWEPT_EDGE",EDGE,{"disambiguationData":[OSD([sQuery(id+"F24.wireOp",EDGE,"E49.0"),sQuery(id+"F24.wireOp",EDGE,"E52.0.right")])]})});
            fillet(context, id + "F28", {"entities" : qUnion([Q0, Q1, Q2, Q3]), "radius" : 1 * mm, "tangentPropagation" : true, "allowEdgeOverflow" : false});
        }
    });
